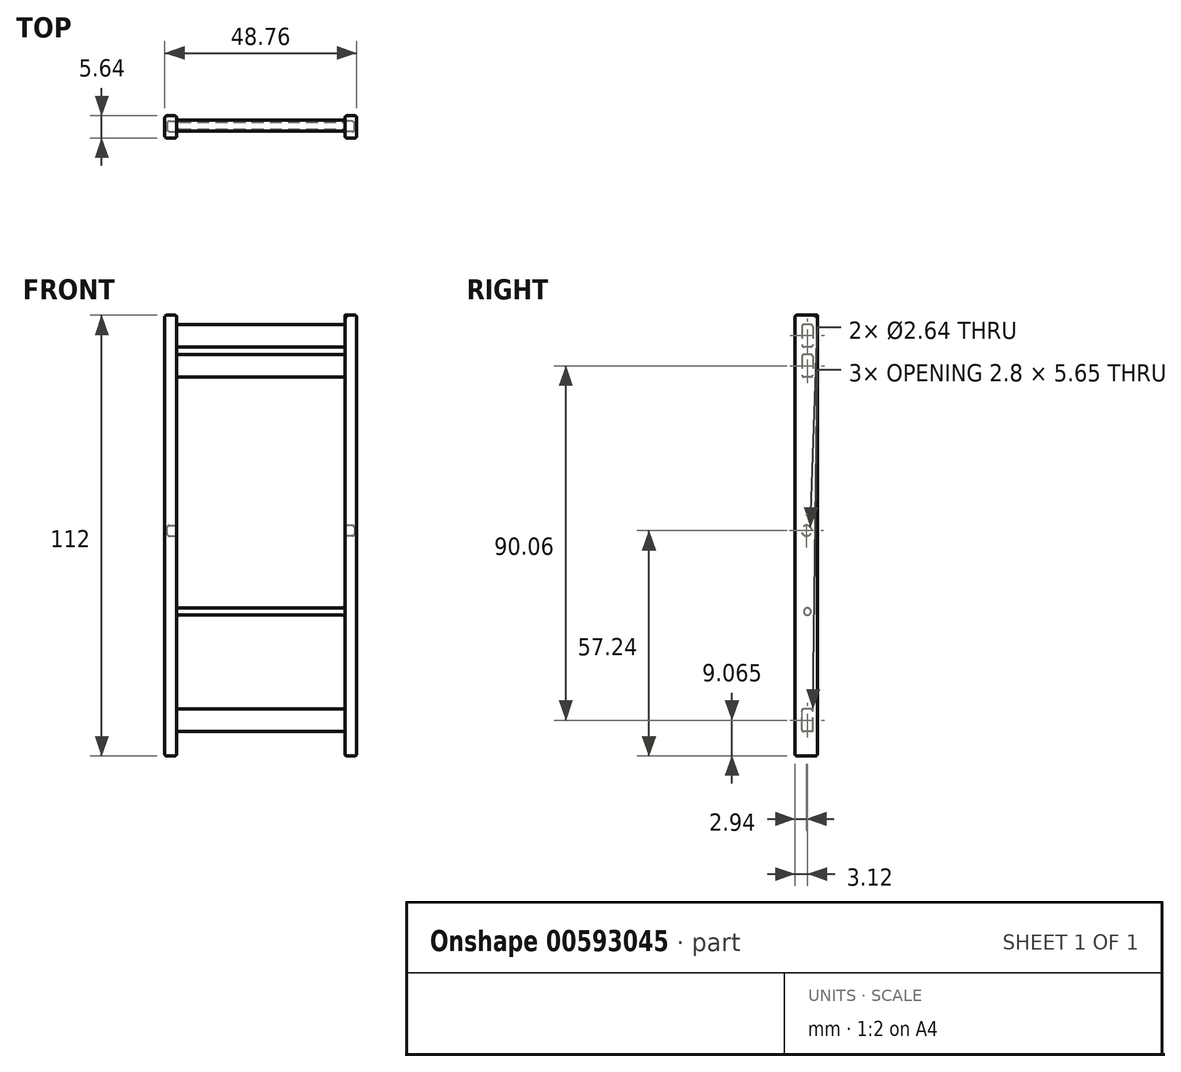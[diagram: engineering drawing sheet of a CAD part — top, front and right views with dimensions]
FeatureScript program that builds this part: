
annotation { "Feature Type Name" : "Feature", "Feature Type Description" : "" }
export const myFeature = defineFeature(function(context is Context, id is Id, definition is map)
    precondition{}
    {
        {
            var Q0;
            Q0=qCreatedBy(makeId("Right.planeOp"),FACE);
            var sketch = newSketch(context, id + "F0", { "sketchPlane" : qUnion([Q0])});
            skLineSegment(sketch, "E0.bottom", {"start": v(2.82, -56) * mm, "end": v(-2.82, -56) * mm});
            skLineSegment(sketch, "E0.top", {"start": v(2.82, 56) * mm, "end": v(-2.82, 56) * mm});
            skLineSegment(sketch, "E0.left", {"start": v(2.82, -56) * mm, "end": v(2.82, 56) * mm});
            skLineSegment(sketch, "E0.right", {"start": v(-2.82, -56) * mm, "end": v(-2.82, 56) * mm});
            skPoint(sketch, "E0.middle", {"position": v(0, 0) * mm});
            skSolve(sketch);
        }
        {
            var Q0;
            Q0=makeQuery(id+"F0.imprint","IMPRINT",FACE,{"disambiguationData":[TD([[makeQuery(id+"F0.imprint","IMPRINT",EDGE,{"derivedFrom":sQuery(id+"F0.wireOp",EDGE,"E0.bottom")}),-1.0]])]});
            extrude(context, id + "F1", {"entities" : qUnion([Q0]), "flatOperationType" : FlatOperationType.REMOVE, "offsetDistance" : 25 * mm, "depth" : 3 * mm, "domain" : OperationDomain.MODEL});
        }
        {
            var Q0;
            Q0=makeQuery(id+"F1.opExtrude","CAP_FACE",FACE,{"disambiguationData":[OSD([sQuery(id+"F0.wireOp",EDGE,"E0.bottom"),sQuery(id+"F0.wireOp",EDGE,"E0.top"),sQuery(id+"F0.wireOp",EDGE,"E0.left"),sQuery(id+"F0.wireOp",EDGE,"E0.right")])],"isStart":true});
            var sketch = newSketch(context, id + "F2", { "sketchPlane" : qUnion([Q0])});
            skLineSegment(sketch, "E1.bottom", {"start": v(-1.7, 53.6) * mm, "end": v(1.1, 53.6) * mm});
            skLineSegment(sketch, "E1.top", {"start": v(-1.7, 47.95) * mm, "end": v(1.1, 47.95) * mm});
            skLineSegment(sketch, "E1.left", {"start": v(-1.7, 53.6) * mm, "end": v(-1.7, 47.95) * mm});
            skLineSegment(sketch, "E1.right", {"start": v(1.1, 53.6) * mm, "end": v(1.1, 47.95) * mm});
            skLineSegment(sketch, "E2.bottom", {"start": v(-1.7, 45.95) * mm, "end": v(1.1, 45.95) * mm});
            skLineSegment(sketch, "E2.top", {"start": v(-1.7, 40.3) * mm, "end": v(1.1, 40.3) * mm});
            skLineSegment(sketch, "E2.left", {"start": v(-1.7, 45.95) * mm, "end": v(-1.7, 40.3) * mm});
            skLineSegment(sketch, "E2.right", {"start": v(1.1, 45.95) * mm, "end": v(1.1, 40.3) * mm});
            skLineSegment(sketch, "E3.bottom", {"start": v(-1.7, -49.76) * mm, "end": v(1.1, -49.76) * mm});
            skLineSegment(sketch, "E3.top", {"start": v(-1.7, -44.1) * mm, "end": v(1.1, -44.1) * mm});
            skLineSegment(sketch, "E3.left", {"start": v(-1.7, -49.76) * mm, "end": v(-1.7, -44.11) * mm});
            skLineSegment(sketch, "E3.right", {"start": v(1.1, -49.76) * mm, "end": v(1.1, -44.1) * mm});
            skCircle(sketch, "E4", {"center": v(-0.32, -19.3) * mm, "radius": 0.9 * mm});
            skSolve(sketch);
        }
        {
            var Q0;
            Q0=qSketchRegion(id+"F2",true);
            extrude(context, id + "F3", {"entities" : qUnion([Q0]), "operationType" : NewBodyOperationType.ADD, "flatOperationType" : FlatOperationType.REMOVE, "offsetDistance" : 25 * mm, "depth" : 42.76 * mm, "domain" : OperationDomain.MODEL});
        }
        {
            var Q0;
            Q0=makeQuery(id+"F3.opExtrude","CAP_FACE",FACE,{"disambiguationData":[OSD([sQuery(id+"F2.wireOp",EDGE,"E1.bottom"),sQuery(id+"F2.wireOp",EDGE,"E1.top"),sQuery(id+"F2.wireOp",EDGE,"E1.left"),sQuery(id+"F2.wireOp",EDGE,"E1.right")])],"isStart":false});
            var sketch = newSketch(context, id + "F4", { "sketchPlane" : qUnion([Q0])});
            skLineSegment(sketch, "E5.bottom", {"start": v(-2.82, 56) * mm, "end": v(2.82, 56) * mm});
            skLineSegment(sketch, "E5.top", {"start": v(-2.82, -56) * mm, "end": v(2.82, -56) * mm});
            skLineSegment(sketch, "E5.left", {"start": v(-2.82, 56) * mm, "end": v(-2.82, -56) * mm});
            skLineSegment(sketch, "E5.right", {"start": v(2.82, 56) * mm, "end": v(2.82, -56) * mm});
            skSolve(sketch);
        }
        {
            var Q0;
            Q0=qSketchRegion(id+"F4",true);
            extrude(context, id + "F5", {"entities" : qUnion([Q0]), "operationType" : NewBodyOperationType.ADD, "flatOperationType" : FlatOperationType.REMOVE, "offsetDistance" : 25 * mm, "depth" : 3 * mm, "domain" : OperationDomain.MODEL});
        }
        {
            var Q0;
            Q0=makeQuery(id+"F1.opExtrude","CAP_FACE",FACE,{"disambiguationData":[OSD([sQuery(id+"F0.wireOp",EDGE,"E0.bottom"),sQuery(id+"F0.wireOp",EDGE,"E0.top"),sQuery(id+"F0.wireOp",EDGE,"E0.left"),sQuery(id+"F0.wireOp",EDGE,"E0.right")])],"isStart":true});
            var sketch = newSketch(context, id + "F6", { "sketchPlane" : qUnion([Q0])});
            skCircle(sketch, "E6", {"center": v(-0.12, 1.24) * mm, "radius": 1.32 * mm});
            skLineSegment(sketch, "E7", {"start": v(0, 56) * mm, "end": v(0, -56) * mm, "construction": true});
            skSolve(sketch);
        }
        {
            var Q0;
            Q0=makeQuery(id+"F6.imprint","IMPRINT",FACE,{"disambiguationData":[TD([[makeQuery(id+"F6.imprint","IMPRINT",EDGE,{"derivedFrom":sQuery(id+"F6.wireOp",EDGE,"E6")}),1.0]])]});
            extrude(context, id + "F7", {"entities" : qUnion([Q0]), "operationType" : NewBodyOperationType.REMOVE, "flatOperationType" : FlatOperationType.REMOVE, "oppositeDirection" : true, "offsetDistance" : 25 * mm, "depth" : 2.4 * mm, "domain" : OperationDomain.MODEL});
        }
        {
            var Q0;
            Q0=makeQuery(id+"F5.opExtrude","CAP_FACE",FACE,{"disambiguationData":[OSD([sQuery(id+"F4.wireOp",EDGE,"E5.bottom"),sQuery(id+"F4.wireOp",EDGE,"E5.top"),sQuery(id+"F4.wireOp",EDGE,"E5.left"),sQuery(id+"F4.wireOp",EDGE,"E5.right")])],"isStart":true});
            var sketch = newSketch(context, id + "F8", { "sketchPlane" : qUnion([Q0])});
            skCircle(sketch, "E8", {"center": v(0.12, 1.24) * mm, "radius": 1.32 * mm});
            skSolve(sketch);
        }
        {
            var Q0;
            Q0=qSketchRegion(id+"F8",true);
            extrude(context, id + "F9", {"entities" : qUnion([Q0]), "operationType" : NewBodyOperationType.REMOVE, "oppositeDirection" : true, "depth" : 2.4 * mm});
        }
        {
            var Q0;
            Q0=makeQuery(id+"F3.opExtrude","CAP_EDGE",EDGE,{"disambiguationData":[OSD([sQuery(id+"F2.wireOp",EDGE,"E2.top")])],"isStart":true});
            var Q1;
            Q1=makeQuery(id+"F3.opExtrude","CAP_EDGE",EDGE,{"disambiguationData":[OSD([sQuery(id+"F2.wireOp",EDGE,"E2.left")])],"isStart":true});
            var Q2;
            Q2=makeQuery(id+"F3.opExtrude","CAP_EDGE",EDGE,{"disambiguationData":[OSD([sQuery(id+"F2.wireOp",EDGE,"E1.top")])],"isStart":true});
            var Q3;
            Q3=makeQuery(id+"F3.opExtrude","CAP_EDGE",EDGE,{"disambiguationData":[OSD([sQuery(id+"F2.wireOp",EDGE,"E1.left")])],"isStart":true});
            var Q4;
            Q4=makeQuery(id+"F3.opExtrude","CAP_EDGE",EDGE,{"disambiguationData":[OSD([sQuery(id+"F2.wireOp",EDGE,"E1.bottom")])],"isStart":true});
            var Q5;
            Q5=makeQuery(id+"F3.opExtrude","CAP_EDGE",EDGE,{"disambiguationData":[OSD([sQuery(id+"F2.wireOp",EDGE,"E1.right")])],"isStart":true});
            var Q6;
            Q6=makeQuery(id+"F3.opExtrude","CAP_EDGE",EDGE,{"disambiguationData":[OSD([sQuery(id+"F2.wireOp",EDGE,"E2.bottom")])],"isStart":true});
            var Q7;
            Q7=makeQuery(id+"F3.opExtrude","CAP_EDGE",EDGE,{"disambiguationData":[OSD([sQuery(id+"F2.wireOp",EDGE,"E2.right")])],"isStart":true});
            var Q8;
            Q8=makeQuery(id+"F3.opExtrude","CAP_EDGE",EDGE,{"disambiguationData":[OSD([sQuery(id+"F2.wireOp",EDGE,"E1.right")])],"isStart":false});
            var Q9;
            Q9=makeQuery(id+"F3.opExtrude","CAP_EDGE",EDGE,{"disambiguationData":[OSD([sQuery(id+"F2.wireOp",EDGE,"E1.bottom")])],"isStart":false});
            var Q10;
            Q10=makeQuery(id+"F3.opExtrude","CAP_EDGE",EDGE,{"disambiguationData":[OSD([sQuery(id+"F2.wireOp",EDGE,"E2.bottom")])],"isStart":false});
            var Q11;
            Q11=makeQuery(id+"F3.opExtrude","CAP_EDGE",EDGE,{"disambiguationData":[OSD([sQuery(id+"F2.wireOp",EDGE,"E2.right")])],"isStart":false});
            var Q12;
            Q12=makeQuery(id+"F3.opExtrude","CAP_EDGE",EDGE,{"disambiguationData":[OSD([sQuery(id+"F2.wireOp",EDGE,"E1.left")])],"isStart":false});
            var Q13;
            Q13=makeQuery(id+"F3.opExtrude","CAP_EDGE",EDGE,{"disambiguationData":[OSD([sQuery(id+"F2.wireOp",EDGE,"E1.top")])],"isStart":false});
            var Q14;
            Q14=makeQuery(id+"F3.opExtrude","CAP_EDGE",EDGE,{"disambiguationData":[OSD([sQuery(id+"F2.wireOp",EDGE,"E2.left")])],"isStart":false});
            var Q15;
            Q15=makeQuery(id+"F3.opExtrude","CAP_EDGE",EDGE,{"disambiguationData":[OSD([sQuery(id+"F2.wireOp",EDGE,"E2.top")])],"isStart":false});
            var Q16;
            Q16=makeQuery(id+"F3.opExtrude","CAP_EDGE",EDGE,{"disambiguationData":[OSD([sQuery(id+"F2.wireOp",EDGE,"E3.bottom")])],"isStart":false});
            var Q17;
            Q17=makeQuery(id+"F3.opExtrude","CAP_EDGE",EDGE,{"disambiguationData":[OSD([sQuery(id+"F2.wireOp",EDGE,"E3.left")])],"isStart":false});
            var Q18;
            Q18=makeQuery(id+"F3.opExtrude","CAP_EDGE",EDGE,{"disambiguationData":[OSD([sQuery(id+"F2.wireOp",EDGE,"E3.bottom")])],"isStart":true});
            var Q19;
            Q19=makeQuery(id+"F3.opExtrude","CAP_EDGE",EDGE,{"disambiguationData":[OSD([sQuery(id+"F2.wireOp",EDGE,"E3.left")])],"isStart":true});
            var Q20;
            Q20=makeQuery(id+"F3.opExtrude","CAP_EDGE",EDGE,{"disambiguationData":[OSD([sQuery(id+"F2.wireOp",EDGE,"E3.right")])],"isStart":false});
            var Q21;
            Q21=makeQuery(id+"F3.opExtrude","CAP_EDGE",EDGE,{"disambiguationData":[OSD([sQuery(id+"F2.wireOp",EDGE,"E3.top")])],"isStart":false});
            var Q22;
            Q22=makeQuery(id+"F3.opExtrude","CAP_EDGE",EDGE,{"disambiguationData":[OSD([sQuery(id+"F2.wireOp",EDGE,"E3.right")])],"isStart":true});
            var Q23;
            Q23=makeQuery(id+"F3.opExtrude","CAP_EDGE",EDGE,{"disambiguationData":[OSD([sQuery(id+"F2.wireOp",EDGE,"E3.top")])],"isStart":true});
            var Q24;
            Q24=makeQuery(id+"F3.opExtrude","SWEPT_FACE",FACE,{"disambiguationData":[OSD([sQuery(id+"F2.wireOp",EDGE,"E4")])]});
            fillet(context, id + "F10", {"entities" : qUnion([Q0, Q1, Q2, Q3, Q4, Q5, Q6, Q7, Q8, Q9, Q10, Q11, Q12, Q13, Q14, Q15, Q16, Q17, Q18, Q19, Q20, Q21, Q22, Q23, Q24]), "radius" : 0.7 * mm, "tangentPropagation" : true, "defaultsChanged" : false, "vertexSettings" : [], "allowEdgeOverflow" : false});
        }
        {
            var Q0;
            Q0=makeQuery(id+"F7.boolean.opBoolean","COPY",EDGE,{"derivedFrom":makeQuery(id+"F7.opExtrude","CAP_EDGE",EDGE,{"disambiguationData":[OSD([sQuery(id+"F6.wireOp",EDGE,"E6")])],"isStart":true})});
            var Q1;
            Q1=makeQuery(id+"F7.boolean.opBoolean","COPY",FACE,{"derivedFrom":makeQuery(id+"F7.opExtrude","CAP_FACE",FACE,{"disambiguationData":[OSD([sQuery(id+"F6.wireOp",EDGE,"E6")])],"isStart":false})});
            var Q2;
            Q2=makeQuery(id+"F9.boolean.opBoolean","COPY",EDGE,{"derivedFrom":makeQuery(id+"F9.opExtrude","CAP_EDGE",EDGE,{"disambiguationData":[OSD([sQuery(id+"F8.wireOp",EDGE,"E8")])],"isStart":true})});
            var Q3;
            Q3=makeQuery(id+"F9.boolean.opBoolean","COPY",EDGE,{"derivedFrom":makeQuery(id+"F9.opExtrude","CAP_EDGE",EDGE,{"disambiguationData":[OSD([sQuery(id+"F8.wireOp",EDGE,"E8")])],"isStart":false})});
            var Q4;
            Q4=makeQuery(id+"F1.opExtrude","CAP_FACE",FACE,{"disambiguationData":[OSD([sQuery(id+"F0.wireOp",EDGE,"E0.bottom"),sQuery(id+"F0.wireOp",EDGE,"E0.top"),sQuery(id+"F0.wireOp",EDGE,"E0.left"),sQuery(id+"F0.wireOp",EDGE,"E0.right")])],"isStart":false});
            var Q5;
            Q5=makeQuery(id+"F1.opExtrude","SWEPT_FACE",FACE,{"disambiguationData":[OSD([sQuery(id+"F0.wireOp",EDGE,"E0.right")])]});
            var Q6;
            Q6=makeQuery(id+"F5.opExtrude","SWEPT_FACE",FACE,{"disambiguationData":[OSD([sQuery(id+"F4.wireOp",EDGE,"E5.right")])]});
            var Q7;
            Q7=makeQuery(id+"F5.opExtrude","CAP_FACE",FACE,{"disambiguationData":[OSD([sQuery(id+"F4.wireOp",EDGE,"E5.bottom"),sQuery(id+"F4.wireOp",EDGE,"E5.top"),sQuery(id+"F4.wireOp",EDGE,"E5.left"),sQuery(id+"F4.wireOp",EDGE,"E5.right")])],"isStart":false});
            var Q8;
            Q8=makeQuery(id+"F3.opExtrude","SWEPT_EDGE",EDGE,{"disambiguationData":[OSD([sQuery(id+"F2.wireOp",EDGE,"E3.bottom"),sQuery(id+"F2.wireOp",EDGE,"E3.right")])]});
            var Q9;
            Q9=makeQuery(id+"F3.opExtrude","SWEPT_EDGE",EDGE,{"disambiguationData":[OSD([sQuery(id+"F2.wireOp",EDGE,"E3.bottom"),sQuery(id+"F2.wireOp",EDGE,"E3.left")])]});
            var Q10;
            Q10=makeQuery(id+"F3.opExtrude","SWEPT_EDGE",EDGE,{"disambiguationData":[OSD([sQuery(id+"F2.wireOp",EDGE,"E3.top"),sQuery(id+"F2.wireOp",EDGE,"E3.right")])]});
            var Q11;
            Q11=makeQuery(id+"F5.opExtrude","SWEPT_FACE",FACE,{"disambiguationData":[OSD([sQuery(id+"F4.wireOp",EDGE,"E5.top")])]});
            var Q12;
            Q12=makeQuery(id+"F1.opExtrude","SWEPT_FACE",FACE,{"disambiguationData":[OSD([sQuery(id+"F0.wireOp",EDGE,"E0.bottom")])]});
            var Q13;
            Q13=makeQuery(id+"F3.opExtrude","SWEPT_EDGE",EDGE,{"disambiguationData":[OSD([sQuery(id+"F2.wireOp",EDGE,"E3.top"),sQuery(id+"F2.wireOp",EDGE,"E3.left")])]});
            var Q14;
            Q14=makeQuery(id+"F5.opExtrude","SWEPT_FACE",FACE,{"disambiguationData":[OSD([sQuery(id+"F4.wireOp",EDGE,"E5.bottom")])]});
            var Q15;
            Q15=makeQuery(id+"F3.opExtrude","SWEPT_EDGE",EDGE,{"disambiguationData":[OSD([sQuery(id+"F2.wireOp",EDGE,"E1.bottom"),sQuery(id+"F2.wireOp",EDGE,"E1.left")])]});
            var Q16;
            Q16=makeQuery(id+"F3.opExtrude","SWEPT_EDGE",EDGE,{"disambiguationData":[OSD([sQuery(id+"F2.wireOp",EDGE,"E1.bottom"),sQuery(id+"F2.wireOp",EDGE,"E1.right")])]});
            var Q17;
            Q17=makeQuery(id+"F3.opExtrude","SWEPT_EDGE",EDGE,{"disambiguationData":[OSD([sQuery(id+"F2.wireOp",EDGE,"E1.top"),sQuery(id+"F2.wireOp",EDGE,"E1.left")])]});
            var Q18;
            Q18=makeQuery(id+"F3.opExtrude","SWEPT_EDGE",EDGE,{"disambiguationData":[OSD([sQuery(id+"F2.wireOp",EDGE,"E2.bottom"),sQuery(id+"F2.wireOp",EDGE,"E2.left")])]});
            var Q19;
            Q19=makeQuery(id+"F3.opExtrude","SWEPT_EDGE",EDGE,{"disambiguationData":[OSD([sQuery(id+"F2.wireOp",EDGE,"E2.top"),sQuery(id+"F2.wireOp",EDGE,"E2.left")])]});
            var Q20;
            Q20=makeQuery(id+"F3.opExtrude","SWEPT_EDGE",EDGE,{"disambiguationData":[OSD([sQuery(id+"F2.wireOp",EDGE,"E2.bottom"),sQuery(id+"F2.wireOp",EDGE,"E2.right")])]});
            var Q21;
            Q21=makeQuery(id+"F3.opExtrude","SWEPT_EDGE",EDGE,{"disambiguationData":[OSD([sQuery(id+"F2.wireOp",EDGE,"E2.top"),sQuery(id+"F2.wireOp",EDGE,"E2.right")])]});
            var Q22;
            Q22=makeQuery(id+"F3.opExtrude","SWEPT_EDGE",EDGE,{"disambiguationData":[OSD([sQuery(id+"F2.wireOp",EDGE,"E1.top"),sQuery(id+"F2.wireOp",EDGE,"E1.right")])]});
            fillet(context, id + "F11", {"entities" : qUnion([Q0, Q1, Q2, Q3, Q4, Q5, Q6, Q7, Q8, Q9, Q10, Q11, Q12, Q13, Q14, Q15, Q16, Q17, Q18, Q19, Q20, Q21, Q22]), "radius" : .5 * mm, "tangentPropagation" : true, "defaultsChanged" : false, "vertexSettings" : [], "allowEdgeOverflow" : false});
        }
        {
            var Q0;
            Q0=makeQuery(id+"F1.opExtrude","CAP_EDGE",EDGE,{"disambiguationData":[OSD([sQuery(id+"F0.wireOp",EDGE,"E0.left")])],"isStart":true});
            var Q1;
            Q1=makeQuery(id+"F5.opExtrude","CAP_EDGE",EDGE,{"disambiguationData":[OSD([sQuery(id+"F4.wireOp",EDGE,"E5.left")])],"isStart":true});
            fillet(context, id + "F12", {"entities" : qUnion([Q0, Q1]), "radius" : .5 * mm, "tangentPropagation" : true, "defaultsChanged" : false, "vertexSettings" : [], "allowEdgeOverflow" : false});
        }
    });
